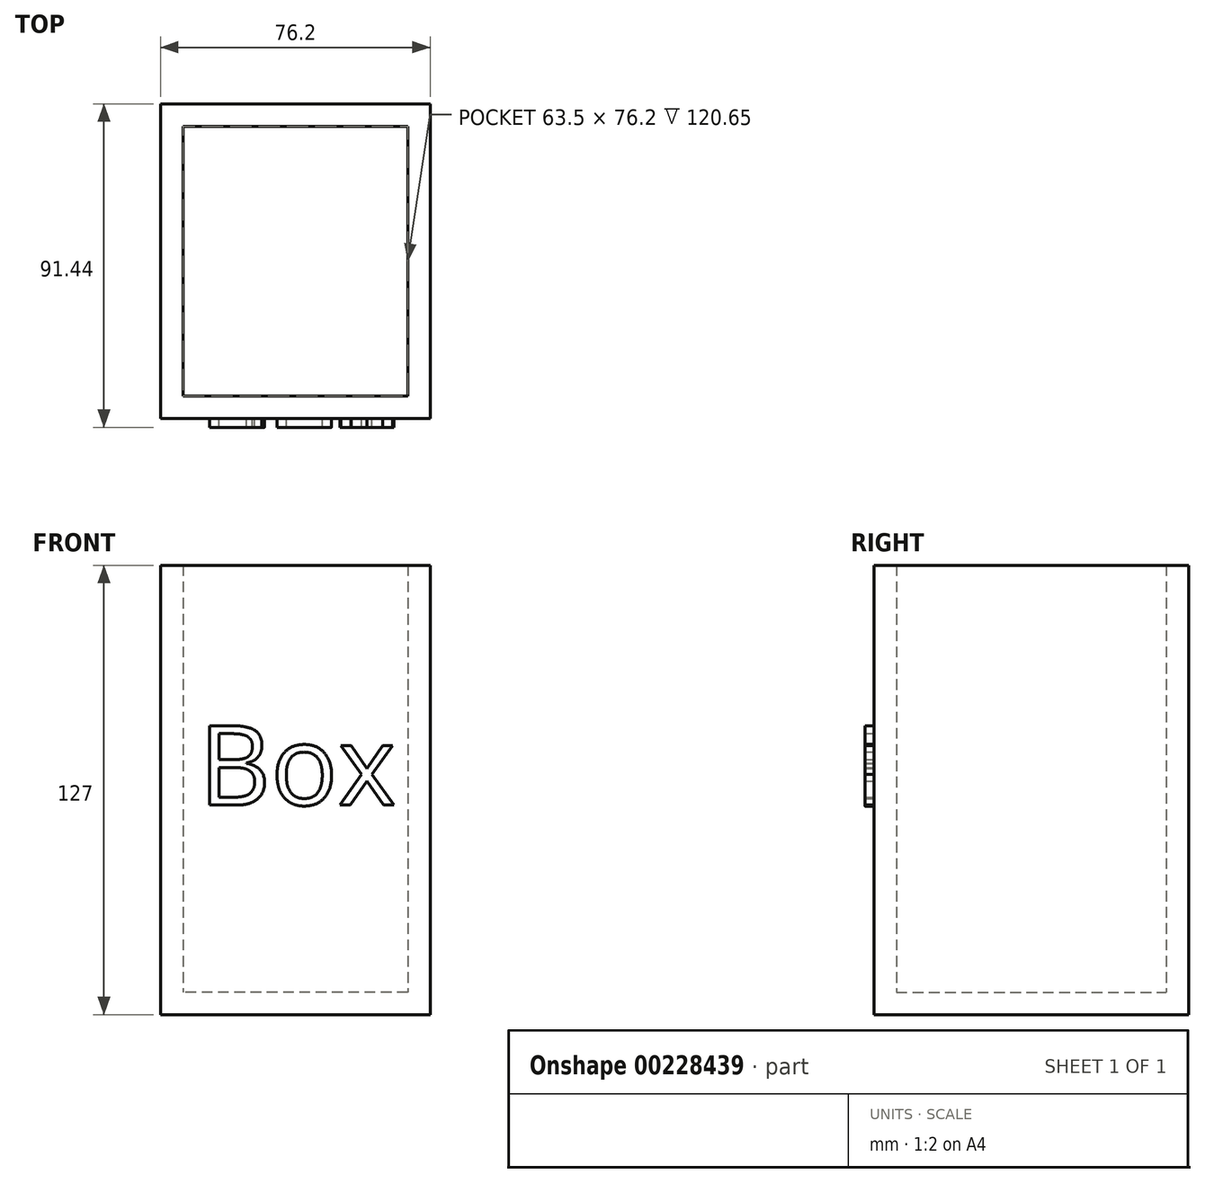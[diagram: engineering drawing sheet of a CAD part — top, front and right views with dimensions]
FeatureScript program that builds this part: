
annotation { "Feature Type Name" : "Feature", "Feature Type Description" : "" }
export const myFeature = defineFeature(function(context is Context, id is Id, definition is map)
    precondition{}
    {
        {
            var Q0;
            Q0=qCreatedBy(makeId("Front.planeOp"),FACE);
            var sketch = newSketch(context, id + "F0", { "sketchPlane" : qUnion([Q0])});
            skLineSegment(sketch, "E0.bottom", {"start": v(38.1, 63.5) * mm, "end": v(-38.1, 63.5) * mm});
            skLineSegment(sketch, "E0.top", {"start": v(38.1, -63.5) * mm, "end": v(-38.1, -63.5) * mm});
            skLineSegment(sketch, "E0.left", {"start": v(38.1, 63.5) * mm, "end": v(38.1, -63.5) * mm});
            skLineSegment(sketch, "E0.right", {"start": v(-38.1, 63.5) * mm, "end": v(-38.1, -63.5) * mm});
            skPoint(sketch, "E0.middle", {"position": v(0, 0) * mm});
            skSolve(sketch);
        }
        {
            var Q0;
            Q0 = qSketchRegion(id + "F0", true);
            extrude(context, id + "F1", {"entities" : qUnion([Q0]), "depth" : 88.9 * mm});
        }
        {
            var Q0;
            Q0=makeQuery(id+"F1.opExtrude","SWEPT_FACE",FACE,{"disambiguationData":[OSD([sQuery(id+"F0.wireOp",EDGE,"E0.bottom")])]});
            shell(context, id + "F2", {"entities" : qUnion([Q0]), "thickness" : 6.35 * mm});
        }
        {
            var Q0;
            Q0=makeQuery(id+"F1.opExtrude","CAP_FACE",FACE,{"disambiguationData":[OSD([sQuery(id+"F0.wireOp",EDGE,"E0.bottom"),sQuery(id+"F0.wireOp",EDGE,"E0.top"),sQuery(id+"F0.wireOp",EDGE,"E0.left"),sQuery(id+"F0.wireOp",EDGE,"E0.right")])],"isStart":false});
            var sketch = newSketch(context, id + "F3", { "sketchPlane" : qUnion([Q0])});
            skText(sketch, "E1", { "text": "Box", "fontName": "OpenSans-Regular.ttf"});
            const initialGuessF3  = {"E1": [-0.0273, -0.00426, 1, 0, 0.0226]};
            skSetInitialGuess(sketch, initialGuessF3);
            skSolve(sketch);
        }
        {
            var Q0;
            Q0 = qSketchRegion(id + "F3", true);
            extrude(context, id + "F4", {"entities" : qUnion([Q0]), "operationType" : NewBodyOperationType.ADD, "depth" : 2.54 * mm});
        }
    });
